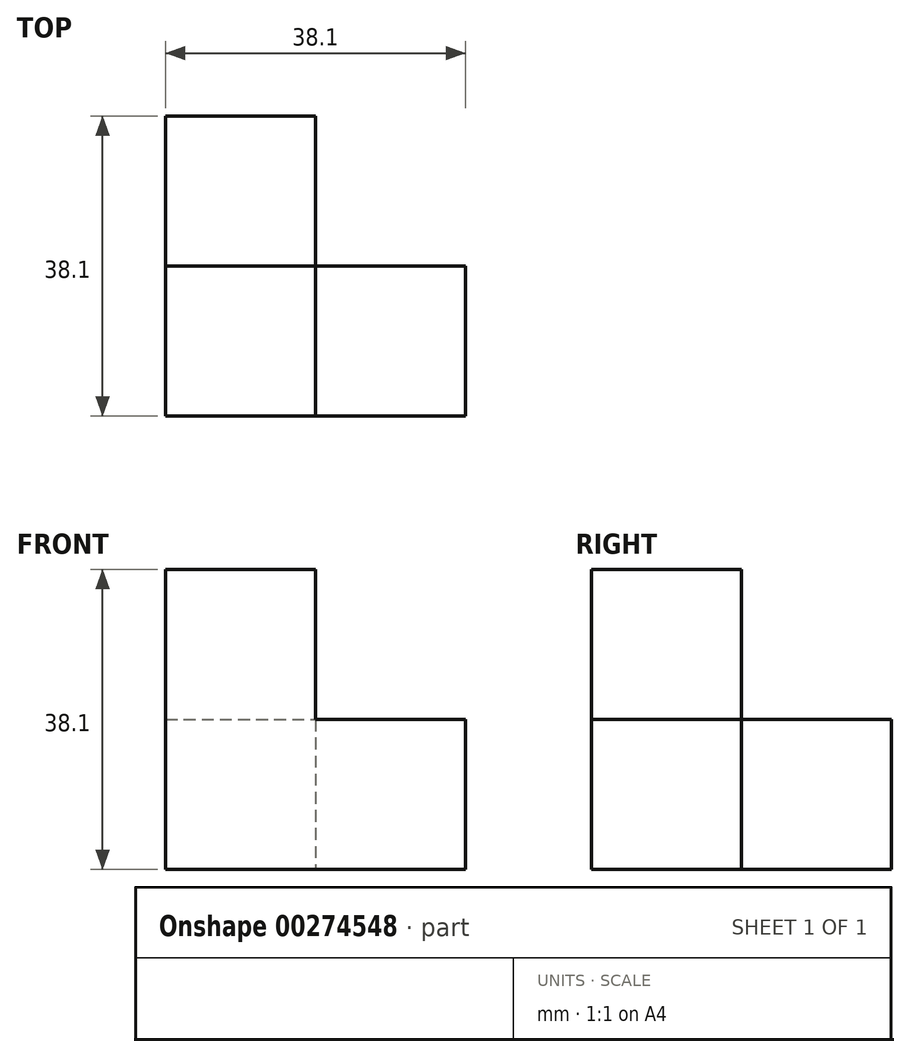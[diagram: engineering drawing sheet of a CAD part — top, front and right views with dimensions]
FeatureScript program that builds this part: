
annotation { "Feature Type Name" : "Feature", "Feature Type Description" : "" }
export const myFeature = defineFeature(function(context is Context, id is Id, definition is map)
    precondition{}
    {
        {
            var Q0;
            Q0=qCreatedBy(makeId("Front.planeOp"),FACE);
            var sketch = newSketch(context, id + "F0", { "sketchPlane" : qUnion([Q0])});
            skLineSegment(sketch, "E0.bottom", {"start": v(-9.53, 9.53) * mm, "end": v(9.53, 9.53) * mm});
            skLineSegment(sketch, "E0.top", {"start": v(-9.53, -9.53) * mm, "end": v(9.53, -9.53) * mm});
            skLineSegment(sketch, "E0.left", {"start": v(-9.53, 9.53) * mm, "end": v(-9.53, -9.53) * mm});
            skLineSegment(sketch, "E0.right", {"start": v(9.53, 9.53) * mm, "end": v(9.53, -9.53) * mm});
            skPoint(sketch, "E0.middle", {"position": v(0, 0) * mm});
            skLineSegment(sketch, "E1.top", {"start": v(-9.53, -28.57) * mm, "end": v(9.53, -28.57) * mm});
            skLineSegment(sketch, "E1.left", {"start": v(-9.53, -9.52) * mm, "end": v(-9.53, -28.57) * mm});
            skLineSegment(sketch, "E1.right", {"start": v(9.53, -9.52) * mm, "end": v(9.53, -28.57) * mm});
            skPoint(sketch, "E1.middle", {"position": v(0, -19.05) * mm});
            skLineSegment(sketch, "E2.bottom", {"start": v(9.52, -9.53) * mm, "end": v(28.57, -9.53) * mm});
            skLineSegment(sketch, "E2.top", {"start": v(9.52, -28.57) * mm, "end": v(28.58, -28.57) * mm});
            skLineSegment(sketch, "E2.left", {"start": v(9.52, -9.52) * mm, "end": v(9.53, -28.57) * mm});
            skLineSegment(sketch, "E2.right", {"start": v(28.57, -9.52) * mm, "end": v(28.57, -28.57) * mm});
            skPoint(sketch, "E2.middle", {"position": v(19.05, -19.05) * mm});
            skSolve(sketch);
        }
        {
            var Q0;
            Q0=makeQuery(id+"F0.imprint","IMPRINT",FACE,{"disambiguationData":[TD([[makeQuery(id+"F0.imprint","IMPRINT",EDGE,{"derivedFrom":sQuery(id+"F0.wireOp",EDGE,"E0.top")}),-1.0]])]});
            var Q1;
            Q1=qCreatedBy(makeId("Top.planeOp"),FACE);
            extrude(context, id + "F1", {"entities" : qUnion([Q0]), "endBound" : BoundingType.SYMMETRIC, "endBoundEntityFace" : qUnion([Q1]), "depth" : 38.1 * mm});
        }
        {
            var Q0;
            Q0 = qSketchRegion(id + "F0", true);
            extrude(context, id + "F2", {"entities" : qUnion([Q0]), "operationType" : NewBodyOperationType.ADD, "depth" : 19.05 * mm});
        }
    });
